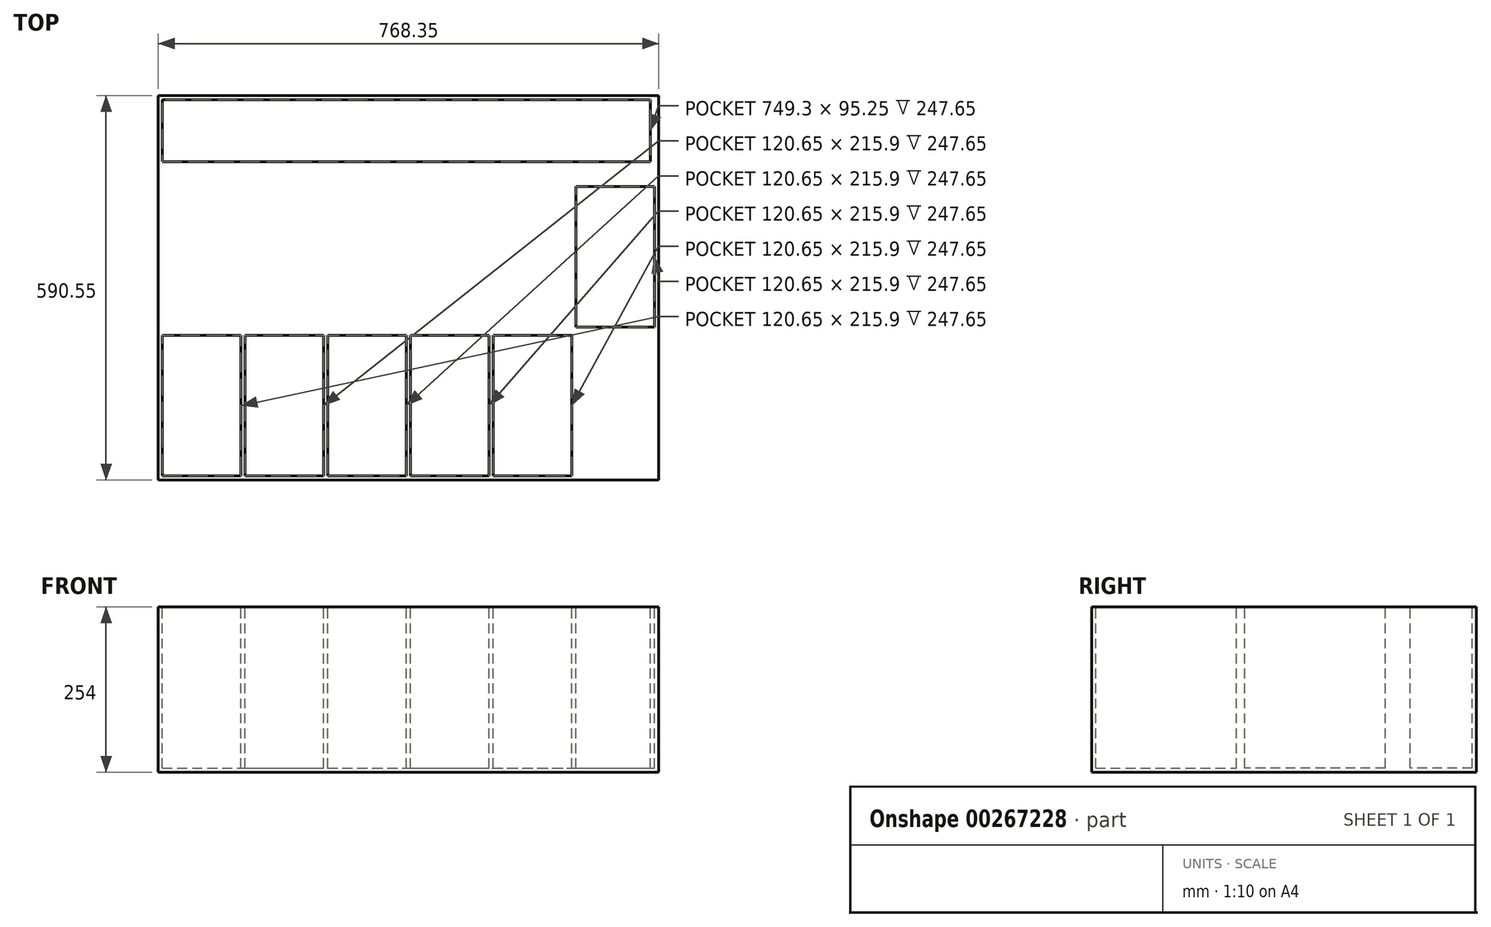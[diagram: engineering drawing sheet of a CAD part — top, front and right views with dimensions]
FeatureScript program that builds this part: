
annotation { "Feature Type Name" : "Feature", "Feature Type Description" : "" }
export const myFeature = defineFeature(function(context is Context, id is Id, definition is map)
    precondition{}
    {
        {
            var Q0;
            Q0=qCreatedBy(makeId("Top.planeOp"),FACE);
            var sketch = newSketch(context, id + "F0", { "sketchPlane" : qUnion([Q0])});
            skLineSegment(sketch, "E0.bottom", {"start": v(-377.4, 315.6) * mm, "end": v(384.6, 315.6) * mm});
            skLineSegment(sketch, "E0.top", {"start": v(-377.4, -268.6) * mm, "end": v(384.6, -268.6) * mm});
            skLineSegment(sketch, "E0.left", {"start": v(-377.4, 315.6) * mm, "end": v(-377.4, -268.6) * mm});
            skLineSegment(sketch, "E0.right", {"start": v(384.6, 315.6) * mm, "end": v(384.6, -268.6) * mm});
            skSolve(sketch);
        }
        {
            var Q0;
            Q0 = qSketchRegion(id + "F0", true);
            extrude(context, id + "F1", {"entities" : qUnion([Q0]), "depth" : 254 * mm});
        }
        {
            var Q0;
            Q0=makeQuery(id+"F1.opExtrude","CAP_FACE",FACE,{"disambiguationData":[OSD([sQuery(id+"F0.wireOp",EDGE,"E0.bottom"),sQuery(id+"F0.wireOp",EDGE,"E0.top"),sQuery(id+"F0.wireOp",EDGE,"E0.left"),sQuery(id+"F0.wireOp",EDGE,"E0.right")])],"isStart":false});
            var sketch = newSketch(context, id + "F2", { "sketchPlane" : qUnion([Q0])});
            skLineSegment(sketch, "E1", {"start": v(-377.4, 295.66) * mm, "end": v(-371.04, 295.66) * mm});
            skLineSegment(sketch, "E2", {"start": v(-371.04, 315.6) * mm, "end": v(-371.04, 309.24) * mm});
            skLineSegment(sketch, "E3.bottom", {"start": v(-371.04, 309.24) * mm, "end": v(378.26, 309.24) * mm});
            skLineSegment(sketch, "E3.top", {"start": v(-371.04, 214) * mm, "end": v(378.26, 214) * mm});
            skLineSegment(sketch, "E3.left", {"start": v(-371.04, 309.24) * mm, "end": v(-371.04, 214) * mm});
            skLineSegment(sketch, "E3.right", {"start": v(378.26, 309.24) * mm, "end": v(378.26, 214) * mm});
            skLineSegment(sketch, "E4", {"start": v(384.6, 277.7) * mm, "end": v(378.26, 277.7) * mm});
            skSolve(sketch);
        }
        {
            var Q0;
            {var subQ3=sQuery(id+"F2.wireOp",EDGE,"E3.bottom");Q0=makeQuery(id+"F2.imprint","IMPRINT",FACE,{"disambiguationData":[TD([[makeQuery(id+"F2.imprint","IMPRINT",EDGE,{"derivedFrom":subQ3}),-1.0]])]});}
            extrude(context, id + "F3", {"entities" : qUnion([Q0]), "operationType" : NewBodyOperationType.REMOVE, "oppositeDirection" : true, "depth" : 247.65 * mm});
        }
        {
            var Q0;
            Q0=makeQuery(id+"F1.opExtrude","CAP_FACE",FACE,{"disambiguationData":[OSD([sQuery(id+"F0.wireOp",EDGE,"E0.bottom"),sQuery(id+"F0.wireOp",EDGE,"E0.top"),sQuery(id+"F0.wireOp",EDGE,"E0.left"),sQuery(id+"F0.wireOp",EDGE,"E0.right")])],"isStart":false});
            var sketch = newSketch(context, id + "F4", { "sketchPlane" : qUnion([Q0])});
            skLineSegment(sketch, "E5.bottom", {"start": v(-371.04, 214) * mm, "end": v(378.26, 214) * mm});
            skLineSegment(sketch, "E5.top", {"start": v(-371.04, 175.9) * mm, "end": v(378.26, 175.9) * mm});
            skLineSegment(sketch, "E5.left", {"start": v(-371.04, 214) * mm, "end": v(-371.04, 175.9) * mm});
            skLineSegment(sketch, "E5.right", {"start": v(378.26, 214) * mm, "end": v(378.26, 175.9) * mm});
            skLineSegment(sketch, "E6.bottom", {"start": v(-371.04, 175.9) * mm, "end": v(-250.4, 175.9) * mm});
            skLineSegment(sketch, "E6.top", {"start": v(-371.04, -40) * mm, "end": v(-250.4, -40) * mm});
            skLineSegment(sketch, "E6.left", {"start": v(-371.04, 175.9) * mm, "end": v(-371.04, -40) * mm});
            skLineSegment(sketch, "E6.right", {"start": v(-250.4, 175.9) * mm, "end": v(-250.4, -40) * mm});
            skLineSegment(sketch, "E7", {"start": v(-250.4, 138.99) * mm, "end": v(-244.04, 138.99) * mm});
            skLineSegment(sketch, "E8.bottom", {"start": v(-244.04, 175.9) * mm, "end": v(-123.4, 175.9) * mm});
            skLineSegment(sketch, "E8.top", {"start": v(-244.04, -40) * mm, "end": v(-123.4, -40) * mm});
            skLineSegment(sketch, "E8.left", {"start": v(-244.04, 175.9) * mm, "end": v(-244.04, -40) * mm});
            skLineSegment(sketch, "E8.right", {"start": v(-123.4, 175.9) * mm, "end": v(-123.4, -40) * mm});
            skLineSegment(sketch, "E9", {"start": v(-123.4, 137.13) * mm, "end": v(-117.04, 137.13) * mm});
            skLineSegment(sketch, "E10.bottom", {"start": v(-117.04, 175.9) * mm, "end": v(3.6, 175.9) * mm});
            skLineSegment(sketch, "E10.top", {"start": v(-117.04, -40) * mm, "end": v(3.6, -40) * mm});
            skLineSegment(sketch, "E10.left", {"start": v(-117.04, 175.9) * mm, "end": v(-117.04, -40) * mm});
            skLineSegment(sketch, "E10.right", {"start": v(3.6, 175.9) * mm, "end": v(3.6, -40) * mm});
            skLineSegment(sketch, "E11", {"start": v(3.6, 139.9) * mm, "end": v(9.96, 139.9) * mm});
            skLineSegment(sketch, "E12.bottom", {"start": v(9.96, 175.9) * mm, "end": v(130.6, 175.9) * mm});
            skLineSegment(sketch, "E12.top", {"start": v(9.96, -40) * mm, "end": v(130.6, -40) * mm});
            skLineSegment(sketch, "E12.left", {"start": v(9.96, 175.9) * mm, "end": v(9.96, -40) * mm});
            skLineSegment(sketch, "E12.right", {"start": v(130.6, 175.9) * mm, "end": v(130.6, -40) * mm});
            skLineSegment(sketch, "E13", {"start": v(130.6, 149.87) * mm, "end": v(136.96, 149.87) * mm});
            skLineSegment(sketch, "E14.bottom", {"start": v(136.96, 175.9) * mm, "end": v(257.6, 175.9) * mm});
            skLineSegment(sketch, "E14.top", {"start": v(136.96, -40) * mm, "end": v(257.6, -40) * mm});
            skLineSegment(sketch, "E14.left", {"start": v(136.96, 175.9) * mm, "end": v(136.96, -40) * mm});
            skLineSegment(sketch, "E14.right", {"start": v(257.6, 175.9) * mm, "end": v(257.6, -40) * mm});
            skLineSegment(sketch, "E15", {"start": v(257.6, 151.04) * mm, "end": v(263.96, 151.04) * mm});
            skLineSegment(sketch, "E16.bottom", {"start": v(263.96, 175.9) * mm, "end": v(384.6, 175.9) * mm});
            skLineSegment(sketch, "E16.top", {"start": v(263.96, -40) * mm, "end": v(384.6, -40) * mm});
            skLineSegment(sketch, "E16.left", {"start": v(263.96, 175.9) * mm, "end": v(263.96, -40) * mm});
            skLineSegment(sketch, "E16.right", {"start": v(384.6, 175.9) * mm, "end": v(384.6, -40) * mm});
            skLineSegment(sketch, "E17.bottom", {"start": v(384.6, 315.6) * mm, "end": v(390.96, 315.6) * mm});
            skLineSegment(sketch, "E17.top", {"start": v(384.6, -268.6) * mm, "end": v(390.96, -268.6) * mm});
            skLineSegment(sketch, "E17.left", {"start": v(384.6, 315.6) * mm, "end": v(384.6, -268.6) * mm});
            skLineSegment(sketch, "E17.right", {"start": v(390.96, 315.6) * mm, "end": v(390.96, -268.6) * mm});
            skLineSegment(sketch, "E18", {"start": v(-342.72, -40) * mm, "end": v(-342.72, -46.36) * mm});
            skLineSegment(sketch, "E19", {"start": v(-342.72, -46.36) * mm, "end": v(375, -46.36) * mm});
            skLineSegment(sketch, "E20.MirrorCS", {"start": v(-250.4, -231.7) * mm, "end": v(-244.04, -231.7) * mm});
            skLineSegment(sketch, "E21.MirrorCS", {"start": v(257.6, -243.76) * mm, "end": v(263.96, -243.76) * mm});
            skLineSegment(sketch, "E22.MirrorCS", {"start": v(3.6, -232.62) * mm, "end": v(9.96, -232.62) * mm});
            skLineSegment(sketch, "E23.MirrorCS", {"start": v(-123.4, -229.84) * mm, "end": v(-117.04, -229.84) * mm});
            skLineSegment(sketch, "E24.MirrorCS", {"start": v(130.6, -242.58) * mm, "end": v(136.96, -242.58) * mm});
            skLineSegment(sketch, "E25.MirrorCS", {"start": v(-244.04, -268.6) * mm, "end": v(-244.04, -52.7) * mm});
            skLineSegment(sketch, "E26.MirrorCS", {"start": v(3.6, -268.6) * mm, "end": v(3.6, -52.7) * mm});
            skLineSegment(sketch, "E27.MirrorCS", {"start": v(-244.04, -52.7) * mm, "end": v(-123.4, -52.7) * mm});
            skLineSegment(sketch, "E28.MirrorCS", {"start": v(130.6, -268.6) * mm, "end": v(130.6, -52.7) * mm});
            skLineSegment(sketch, "E29.MirrorCS", {"start": v(136.96, -268.6) * mm, "end": v(136.96, -52.7) * mm});
            skLineSegment(sketch, "E30.MirrorCS", {"start": v(384.6, -268.6) * mm, "end": v(384.6, -52.7) * mm});
            skLineSegment(sketch, "E31.MirrorCS", {"start": v(263.96, -268.6) * mm, "end": v(384.6, -268.6) * mm});
            skLineSegment(sketch, "E32.MirrorCS", {"start": v(9.96, -52.7) * mm, "end": v(130.6, -52.7) * mm});
            skLineSegment(sketch, "E33.MirrorCS", {"start": v(136.96, -52.7) * mm, "end": v(257.6, -52.7) * mm});
            skLineSegment(sketch, "E34.MirrorCS", {"start": v(9.96, -268.6) * mm, "end": v(130.6, -268.6) * mm});
            skLineSegment(sketch, "E35.MirrorCS", {"start": v(-117.04, -268.6) * mm, "end": v(-117.04, -52.7) * mm});
            skLineSegment(sketch, "E36.MirrorCS", {"start": v(136.96, -268.6) * mm, "end": v(257.6, -268.6) * mm});
            skLineSegment(sketch, "E37.MirrorCS", {"start": v(-244.04, -268.6) * mm, "end": v(-123.4, -268.6) * mm});
            skLineSegment(sketch, "E38.MirrorCS", {"start": v(263.96, -268.6) * mm, "end": v(263.96, -52.7) * mm});
            skLineSegment(sketch, "E39.MirrorCS", {"start": v(-123.4, -268.6) * mm, "end": v(-123.4, -52.7) * mm});
            skLineSegment(sketch, "E40.MirrorCS", {"start": v(263.96, -52.7) * mm, "end": v(384.6, -52.7) * mm});
            skLineSegment(sketch, "E41.MirrorCS", {"start": v(-117.04, -52.7) * mm, "end": v(3.6, -52.7) * mm});
            skLineSegment(sketch, "E42.MirrorCS", {"start": v(-117.04, -268.6) * mm, "end": v(3.6, -268.6) * mm});
            skLineSegment(sketch, "E43.MirrorCS", {"start": v(9.96, -268.6) * mm, "end": v(9.96, -52.7) * mm});
            skLineSegment(sketch, "E44.MirrorCS", {"start": v(257.6, -268.6) * mm, "end": v(257.6, -52.7) * mm});
            skLineSegment(sketch, "E45.MirrorCS", {"start": v(-250.4, -268.6) * mm, "end": v(-250.4, -52.7) * mm});
            skLineSegment(sketch, "E46.MirrorCS", {"start": v(-371.04, -268.6) * mm, "end": v(-371.04, -52.7) * mm});
            skLineSegment(sketch, "E47.MirrorCS", {"start": v(-371.04, -52.7) * mm, "end": v(-250.4, -52.7) * mm});
            skLineSegment(sketch, "E48.MirrorCS", {"start": v(-371.04, -268.6) * mm, "end": v(-250.4, -268.6) * mm});
            skLineSegment(sketch, "E49.bottom", {"start": v(-377.4, -268.6) * mm, "end": v(390.96, -268.6) * mm});
            skLineSegment(sketch, "E49.top", {"start": v(-377.4, -274.96) * mm, "end": v(390.96, -274.96) * mm});
            skLineSegment(sketch, "E49.left", {"start": v(-377.4, -268.6) * mm, "end": v(-377.4, -274.96) * mm});
            skLineSegment(sketch, "E49.right", {"start": v(390.96, -268.6) * mm, "end": v(390.96, -274.96) * mm});
            skSolve(sketch);
        }
        {
            var Q0;
            {var subQ3=sQuery(id+"F4.wireOp",EDGE,"E17.bottom");Q0=makeQuery(id+"F4.imprint","IMPRINT",FACE,{"disambiguationData":[TD([[makeQuery(id+"F4.imprint","IMPRINT",EDGE,{"derivedFrom":subQ3}),-1.0]])]});}
            extrude(context, id + "F5", {"entities" : qUnion([Q0]), "operationType" : NewBodyOperationType.ADD, "oppositeDirection" : true, "depth" : 254 * mm});
        }
        {
            var Q0;
            Q0=makeQuery(id+"F4.imprint","IMPRINT",FACE,{"disambiguationData":[TD([[makeQuery(id+"F4.imprint","IMPRINT",EDGE,{"derivedFrom":sQuery(id+"F4.wireOp",EDGE,"E49.top")}),1.0]])]});
            extrude(context, id + "F6", {"entities" : qUnion([Q0]), "operationType" : NewBodyOperationType.ADD, "oppositeDirection" : true, "depth" : 254 * mm});
        }
        {
            var Q0;
            {var subQ4=sQuery(id+"F4.wireOp",EDGE,"E27.MirrorCS");Q0=makeQuery(id+"F4.imprint","IMPRINT",FACE,{"disambiguationData":[TD([[makeQuery(id+"F4.imprint","IMPRINT",EDGE,{"derivedFrom":subQ4}),-1.0]])]});}
            var Q1;
            {var subQ2=sQuery(id+"F4.wireOp",EDGE,"E41.MirrorCS");Q1=makeQuery(id+"F4.imprint","IMPRINT",FACE,{"disambiguationData":[TD([[makeQuery(id+"F4.imprint","IMPRINT",EDGE,{"derivedFrom":subQ2}),-1.0]])]});}
            var Q2;
            {var subQ0=sQuery(id+"F4.wireOp",EDGE,"E32.MirrorCS");Q2=makeQuery(id+"F4.imprint","IMPRINT",FACE,{"disambiguationData":[TD([[makeQuery(id+"F4.imprint","IMPRINT",EDGE,{"derivedFrom":subQ0}),-1.0]])]});}
            var Q3;
            {var subQ0=sQuery(id+"F4.wireOp",EDGE,"E33.MirrorCS");Q3=makeQuery(id+"F4.imprint","IMPRINT",FACE,{"disambiguationData":[TD([[makeQuery(id+"F4.imprint","IMPRINT",EDGE,{"derivedFrom":subQ0}),-1.0]])]});}
            var Q4;
            {var subQ4=sQuery(id+"F4.wireOp",EDGE,"E30.MirrorCS");Q4=makeQuery(id+"F4.imprint","IMPRINT",FACE,{"disambiguationData":[TD([[makeQuery(id+"F4.imprint","IMPRINT",EDGE,{"derivedFrom":subQ4}),-1.0]])]});}
            var Q5;
            {var subQ2=sQuery(id+"F4.wireOp",EDGE,"E14.bottom");Q5=makeQuery(id+"F4.imprint","IMPRINT",FACE,{"disambiguationData":[TD([[makeQuery(id+"F4.imprint","IMPRINT",EDGE,{"derivedFrom":subQ2}),-1.0]])]});}
            var Q6;
            {var subQ2=sQuery(id+"F4.wireOp",EDGE,"E12.bottom");Q6=makeQuery(id+"F4.imprint","IMPRINT",FACE,{"disambiguationData":[TD([[makeQuery(id+"F4.imprint","IMPRINT",EDGE,{"derivedFrom":subQ2}),-1.0]])]});}
            var Q7;
            {var subQ4=sQuery(id+"F4.wireOp",EDGE,"E16.top");Q7=makeQuery(id+"F4.imprint","IMPRINT",FACE,{"disambiguationData":[TD([[makeQuery(id+"F4.imprint","IMPRINT",EDGE,{"derivedFrom":subQ4}),1.0]])]});}
            var Q8;
            {var subQ3=sQuery(id+"F4.wireOp",EDGE,"E10.bottom");Q8=makeQuery(id+"F4.imprint","IMPRINT",FACE,{"disambiguationData":[TD([[makeQuery(id+"F4.imprint","IMPRINT",EDGE,{"derivedFrom":subQ3}),-1.0]])]});}
            var Q9;
            {var subQ2=sQuery(id+"F4.wireOp",EDGE,"E8.bottom");Q9=makeQuery(id+"F4.imprint","IMPRINT",FACE,{"disambiguationData":[TD([[makeQuery(id+"F4.imprint","IMPRINT",EDGE,{"derivedFrom":subQ2}),-1.0]])]});}
            var Q10;
            {var subQ4=sQuery(id+"F4.wireOp",EDGE,"E6.bottom");Q10=makeQuery(id+"F4.imprint","IMPRINT",FACE,{"disambiguationData":[TD([[makeQuery(id+"F4.imprint","IMPRINT",EDGE,{"derivedFrom":subQ4}),-1.0]])]});}
            var Q11;
            {var subQ1=sQuery(id+"F4.wireOp",EDGE,"E46.MirrorCS");Q11=makeQuery(id+"F4.imprint","IMPRINT",FACE,{"disambiguationData":[TD([[makeQuery(id+"F4.imprint","IMPRINT",EDGE,{"derivedFrom":subQ1}),-1.0]])]});}
            extrude(context, id + "F7", {"entities" : qUnion([Q0, Q1, Q2, Q3, Q4, Q5, Q6, Q7, Q8, Q9, Q10, Q11]), "operationType" : NewBodyOperationType.REMOVE, "oppositeDirection" : true, "depth" : 247.65 * mm});
        }
    });
